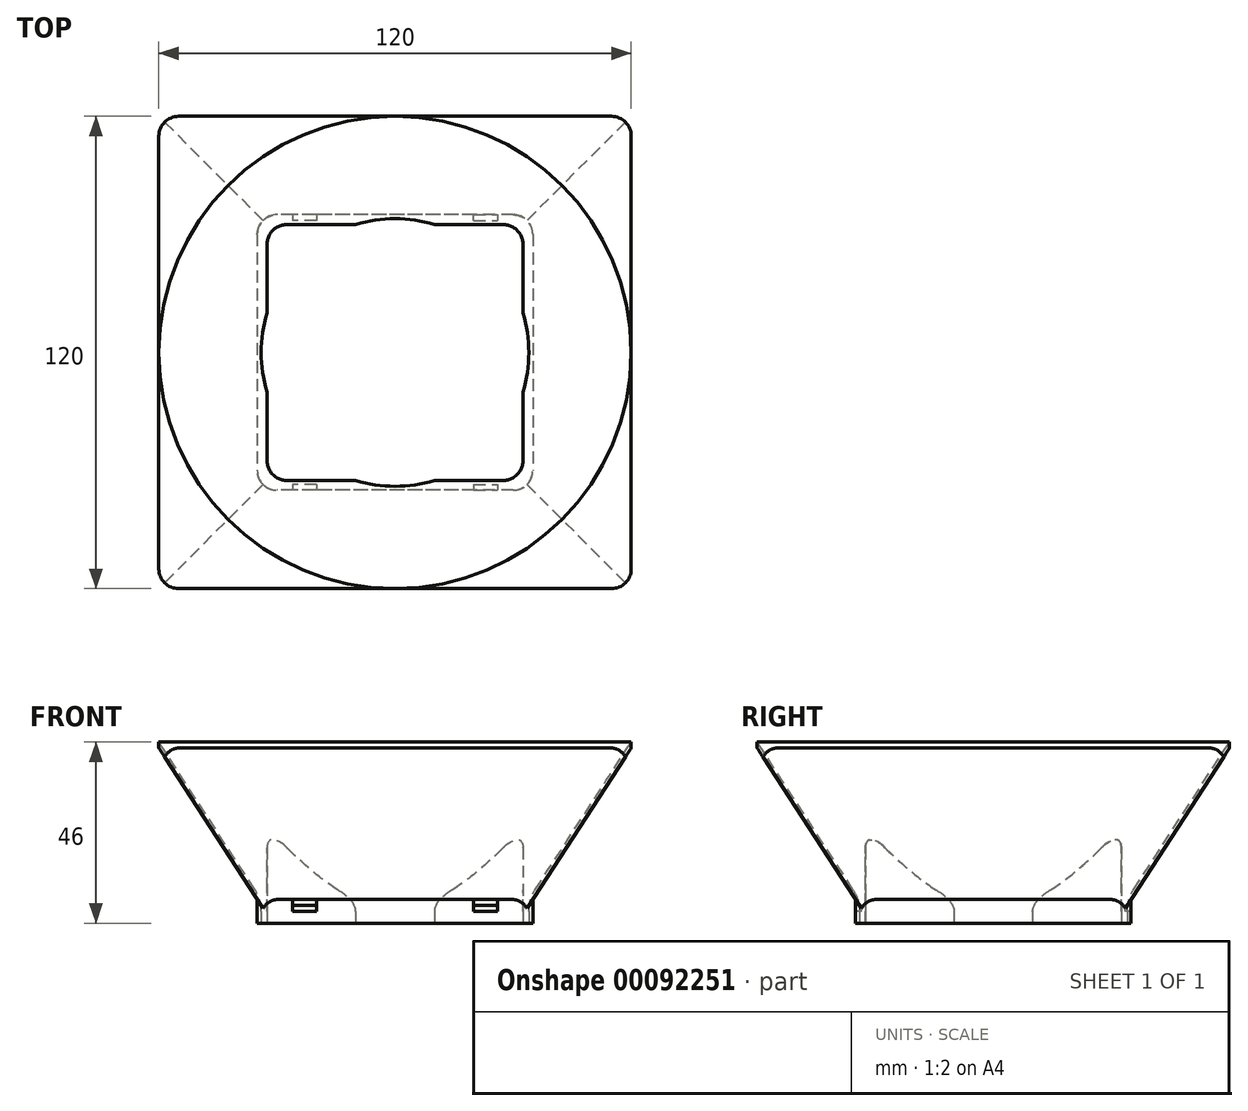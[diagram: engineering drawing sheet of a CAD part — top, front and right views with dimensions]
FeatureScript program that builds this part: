
annotation { "Feature Type Name" : "Feature", "Feature Type Description" : "" }
export const myFeature = defineFeature(function(context is Context, id is Id, definition is map)
    precondition{}
    {
        {
            var Q0;
            Q0=qCreatedBy(makeId("Top.planeOp"),FACE);
            var sketch = newSketch(context, id + "F0", { "sketchPlane" : qUnion([Q0])});
            skLineSegment(sketch, "E0.bottom", {"start": v(35, 35) * mm, "end": v(-35, 35) * mm});
            skLineSegment(sketch, "E0.top", {"start": v(35, -35) * mm, "end": v(-35, -35) * mm});
            skLineSegment(sketch, "E0.left", {"start": v(35, 35) * mm, "end": v(35, -35) * mm});
            skLineSegment(sketch, "E0.right", {"start": v(-35, 35) * mm, "end": v(-35, -35) * mm});
            skPoint(sketch, "E0.middle", {"position": v(0, 0) * mm});
            skSolve(sketch);
        }
        {
            var Q0;
            Q0 = qSketchRegion(id + "F0", true);
            extrude(context, id + "F1", {"entities" : qUnion([Q0]), "depth" : 6 * mm});
        }
        {
            var Q0;
            Q0=makeQuery(id+"F1.opExtrude","CAP_FACE",FACE,{"disambiguationData":[OSD([sQuery(id+"F0.wireOp",EDGE,"E0.bottom"),sQuery(id+"F0.wireOp",EDGE,"E0.top"),sQuery(id+"F0.wireOp",EDGE,"E0.left"),sQuery(id+"F0.wireOp",EDGE,"E0.right")])],"isStart":true});
            var sketch = newSketch(context, id + "F2", { "sketchPlane" : qUnion([Q0])});
            skPoint(sketch, "E1", {"position": v(0, 0) * mm});
            skSolve(sketch);
        }
        {
            var Q0;
            Q0=sQuery(id+"F2.wireOp",VERTEX,"E1");
            var Q1;
            Q1=makeQuery(id+"F1.opExtrude","SWEPT_BODY",BODY,{"disambiguationData":[OSD([sQuery(id+"F0.wireOp",EDGE,"E0.bottom"),sQuery(id+"F0.wireOp",EDGE,"E0.top"),sQuery(id+"F0.wireOp",EDGE,"E0.left"),sQuery(id+"F0.wireOp",EDGE,"E0.right")])]});
            hole(context, id + "F3", {"style" : HoleStyle.SIMPLE, "endStyle" : HoleEndStyle.THROUGH, "holeDiameter" : 68 * mm, "locations" : qUnion([Q0]), "scope" : qUnion([Q1]), "isTappedThrough" : true});
        }
        {
            var Q0;
            Q0=makeQuery(id+"F1.opExtrude","CAP_FACE",FACE,{"disambiguationData":[OSD([sQuery(id+"F0.wireOp",EDGE,"E0.bottom"),sQuery(id+"F0.wireOp",EDGE,"E0.top"),sQuery(id+"F0.wireOp",EDGE,"E0.left"),sQuery(id+"F0.wireOp",EDGE,"E0.right")])],"isStart":false});
            var sketch = newSketch(context, id + "F4", { "sketchPlane" : qUnion([Q0])});
            skLineSegment(sketch, "E2.bottom", {"start": v(-60, -60) * mm, "end": v(60, -60) * mm});
            skLineSegment(sketch, "E2.top", {"start": v(-60, 60) * mm, "end": v(60, 60) * mm});
            skLineSegment(sketch, "E2.left", {"start": v(-60, -60) * mm, "end": v(-60, 60) * mm});
            skLineSegment(sketch, "E2.right", {"start": v(60, -60) * mm, "end": v(60, 60) * mm});
            skPoint(sketch, "E2.middle", {"position": v(0, 0) * mm});
            skSolve(sketch);
        }
        {
            var Q0;
            Q0=makeQuery(id+"F4.imprint","IMPRINT",FACE,{"disambiguationData":[TD([[makeQuery(id+"F4.imprint","IMPRINT",EDGE,{"derivedFrom":sQuery(id+"F4.wireOp",EDGE,"E2.bottom")}),1.0]])]});
            var Q1;
            {var subQ3=sQuery(id+"F0.wireOp",EDGE,"E0.bottom");Q1=makeQuery(id+"F4.imprint","IMPRINT",FACE,{"disambiguationData":[TD([[makeQuery(id+"F4.imprint","IMPRINT",EDGE,{"derivedFrom":makeQuery(id+"F1.opExtrude","CAP_EDGE",EDGE,{"disambiguationData":[OSD([subQ3])],"isStart":false})}),1.0]])]});}
            extrude(context, id + "F5", {"entities" : qUnion([Q0, Q1]), "operationType" : NewBodyOperationType.ADD, "depth" : 40 * mm});
        }
        {
            var Q0;
            Q0=makeQuery(id+"F5.opExtrude","CAP_EDGE",EDGE,{"disambiguationData":[OSD([sQuery(id+"F4.wireOp",EDGE,"E2.bottom")])],"isStart":true});
            var Q1;
            Q1=makeQuery(id+"F5.opExtrude","CAP_EDGE",EDGE,{"disambiguationData":[OSD([sQuery(id+"F4.wireOp",EDGE,"E2.right")])],"isStart":true});
            var Q2;
            Q2=makeQuery(id+"F5.opExtrude","CAP_EDGE",EDGE,{"disambiguationData":[OSD([sQuery(id+"F4.wireOp",EDGE,"E2.top")])],"isStart":true});
            var Q3;
            Q3=makeQuery(id+"F5.opExtrude","CAP_EDGE",EDGE,{"disambiguationData":[OSD([sQuery(id+"F4.wireOp",EDGE,"E2.left")])],"isStart":true});
            chamfer(context, id + "F6", {"entities" : qUnion([Q0, Q1, Q2, Q3]), "chamferType" : ChamferType.TWO_OFFSETS, "width1" : 38.5 * mm, "oppositeDirection" : false, "width2" : 25 * mm, "tangentPropagation" : true});
        }
        {
            var Q0;
            Q0=makeQuery(id+"F5.opExtrude","CAP_EDGE",EDGE,{"disambiguationData":[OSD([sQuery(id+"F0.wireOp",EDGE,"E0.bottom"),sQuery(id+"F0.wireOp",EDGE,"E0.top"),sQuery(id+"F0.wireOp",EDGE,"E0.left"),sQuery(id+"F0.wireOp",EDGE,"E0.right"),sQuery(id+"F3.hole-0.sketch.wireOp",EDGE,"core_line_2")])],"isStart":false});
            chamfer(context, id + "F7", {"entities" : qUnion([Q0]), "chamferType" : ChamferType.TWO_OFFSETS, "width1" : 26 * mm, "oppositeDirection" : false, "width2" : 40 * mm, "tangentPropagation" : true});
        }
        {
            var Q0;
            {var subQ0=sQuery(id+"F3.hole-0.sketch.wireOp",EDGE,"core_line_2");var subQ1=sQuery(id+"F0.wireOp",EDGE,"E0.right");var subQ2=sQuery(id+"F0.wireOp",EDGE,"E0.left");var subQ3=sQuery(id+"F0.wireOp",EDGE,"E0.top");var subQ4=sQuery(id+"F0.wireOp",EDGE,"E0.bottom");Q0=makeQuery(id+"F7.opChamfer","BLEND_EDGE",EDGE,{"blendedFrom":[makeQuery(id+"F5.opExtrude","CAP_EDGE",EDGE,{"disambiguationData":[OSD([subQ4,subQ3,subQ2,subQ1,subQ0])],"isStart":false}),makeQuery(id+"F5.boolean.opBoolean","MERGE",FACE,{"derivedFrom":[makeQuery(id+"F3.hole-0.boolean.opBoolean","COPY",FACE,{"derivedFrom":makeQuery(id+"F3.hole-0.opRevolve","SWEPT_FACE",FACE,{"disambiguationData":[OSD([subQ0])]})}),makeQuery(id+"F5.opExtrude","SWEPT_FACE",FACE,{"disambiguationData":[OSD([subQ4,subQ3,subQ2,subQ1,subQ0])]})]})],"blendedInto":[makeQuery(id+"F5.boolean.opBoolean","MERGE",FACE,{"derivedFrom":[makeQuery(id+"F3.hole-0.boolean.opBoolean","COPY",FACE,{"derivedFrom":makeQuery(id+"F3.hole-0.opRevolve","SWEPT_FACE",FACE,{"disambiguationData":[OSD([subQ0])]})}),makeQuery(id+"F5.opExtrude","SWEPT_FACE",FACE,{"disambiguationData":[OSD([subQ4,subQ3,subQ2,subQ1,subQ0])]})]})]});}
            fillet(context, id + "F8", {"entities" : qUnion([Q0]), "radius" : 10 * mm, "tangentPropagation" : true, "allowEdgeOverflow" : false});
        }
        {
            var Q0;
            Q0=makeQuery(id+"F1.opExtrude","SWEPT_FACE",FACE,{"disambiguationData":[OSD([sQuery(id+"F0.wireOp",EDGE,"E0.top")])]});
            var sketch = newSketch(context, id + "F9", { "sketchPlane" : qUnion([Q0])});
            skLineSegment(sketch, "E3.bottom", {"start": v(-20, 3) * mm, "end": v(-26, 3) * mm});
            skLineSegment(sketch, "E3.top", {"start": v(-20, 6) * mm, "end": v(-26, 6) * mm});
            skLineSegment(sketch, "E3.left", {"start": v(-20, 3) * mm, "end": v(-20, 6) * mm});
            skLineSegment(sketch, "E3.right", {"start": v(-26, 3) * mm, "end": v(-26, 6) * mm});
            skPoint(sketch, "E3.middle", {"position": v(-23, 4.5) * mm});
            skLineSegment(sketch, "E4.bottom", {"start": v(20, 3) * mm, "end": v(26, 3) * mm});
            skLineSegment(sketch, "E4.top", {"start": v(20, 6) * mm, "end": v(26, 6) * mm});
            skLineSegment(sketch, "E4.left", {"start": v(20, 3) * mm, "end": v(20, 6) * mm});
            skLineSegment(sketch, "E4.right", {"start": v(26, 3) * mm, "end": v(26, 6) * mm});
            skPoint(sketch, "E4.middle", {"position": v(23, 4.5) * mm});
            skSolve(sketch);
        }
        {
            var Q0;
            Q0=makeQuery(id+"F9.imprint","IMPRINT",FACE,{"disambiguationData":[TD([[makeQuery(id+"F9.imprint","IMPRINT",EDGE,{"derivedFrom":sQuery(id+"F9.wireOp",EDGE,"E3.bottom")}),-1.0]])]});
            var Q1;
            Q1=makeQuery(id+"F9.imprint","IMPRINT",FACE,{"disambiguationData":[TD([[makeQuery(id+"F9.imprint","IMPRINT",EDGE,{"derivedFrom":sQuery(id+"F9.wireOp",EDGE,"E4.bottom")}),1.0]])]});
            extrude(context, id + "F10", {"entities" : qUnion([Q0, Q1]), "operationType" : NewBodyOperationType.REMOVE, "oppositeDirection" : true, "depth" : 1.5 * mm});
        }
        {
            var Q0;
            Q0=makeQuery(id+"F10.boolean.opBoolean","COPY",FACE,{"derivedFrom":makeQuery(id+"F10.opExtrude","CAP_FACE",FACE,{"disambiguationData":[OSD([sQuery(id+"F9.wireOp",EDGE,"E3.bottom"),sQuery(id+"F9.wireOp",EDGE,"E3.top"),sQuery(id+"F9.wireOp",EDGE,"E3.left"),sQuery(id+"F9.wireOp",EDGE,"E3.right")])],"isStart":false})});
            var Q1;
            Q1=makeQuery(id+"F10.boolean.opBoolean","COPY",FACE,{"derivedFrom":makeQuery(id+"F10.opExtrude","CAP_FACE",FACE,{"disambiguationData":[OSD([sQuery(id+"F9.wireOp",EDGE,"E4.bottom"),sQuery(id+"F9.wireOp",EDGE,"E4.top"),sQuery(id+"F9.wireOp",EDGE,"E4.left"),sQuery(id+"F9.wireOp",EDGE,"E4.right")])],"isStart":false})});
            extrude(context, id + "F11", {"entities" : qUnion([Q0, Q1]), "operationType" : NewBodyOperationType.REMOVE, "oppositeDirection" : true, "depth" : 70 * mm, "hasSecondDirection" : true, "secondDirectionOppositeDirection" : true, "secondDirectionDepth" : 67 * mm});
        }
        {
            var Q0;
            Q0=makeQuery(id+"F1.opExtrude","CAP_FACE",FACE,{"disambiguationData":[OSD([sQuery(id+"F0.wireOp",EDGE,"E0.bottom"),sQuery(id+"F0.wireOp",EDGE,"E0.top"),sQuery(id+"F0.wireOp",EDGE,"E0.left"),sQuery(id+"F0.wireOp",EDGE,"E0.right")])],"isStart":true});
            var sketch = newSketch(context, id + "F12", { "sketchPlane" : qUnion([Q0])});
            skLineSegment(sketch, "E5.bottom", {"start": v(-27.5, -32.5) * mm, "end": v(27.5, -32.5) * mm});
            skLineSegment(sketch, "E5.top", {"start": v(-27.5, 32.5) * mm, "end": v(27.5, 32.5) * mm});
            skLineSegment(sketch, "E5.left", {"start": v(-32.5, -27.5) * mm, "end": v(-32.5, 27.5) * mm});
            skLineSegment(sketch, "E5.right", {"start": v(32.5, -27.5) * mm, "end": v(32.5, 27.5) * mm});
            skPoint(sketch, "E5.middle", {"position": v(0, 0) * mm});
            skPoint(sketch, "E6.visualSharp", {"position": v(-32.5, 32.5) * mm});
            skArc(sketch, "E6.filletArc", {"start": v(-27.5, 32.5) * mm, "mid": v(-31.04, 31.04) * mm, "end": v(-32.5, 27.5) * mm});
            skPoint(sketch, "E7.visualSharp", {"position": v(32.5, 32.5) * mm});
            skArc(sketch, "E7.filletArc", {"start": v(32.5, 27.5) * mm, "mid": v(31.04, 31.04) * mm, "end": v(27.5, 32.5) * mm});
            skPoint(sketch, "E8.visualSharp", {"position": v(32.5, -32.5) * mm});
            skArc(sketch, "E8.filletArc", {"start": v(27.5, -32.5) * mm, "mid": v(31.04, -31.04) * mm, "end": v(32.5, -27.5) * mm});
            skPoint(sketch, "E9.visualSharp", {"position": v(-32.5, -32.5) * mm});
            skArc(sketch, "E9.filletArc", {"start": v(-32.5, -27.5) * mm, "mid": v(-31.04, -31.04) * mm, "end": v(-27.5, -32.5) * mm});
            skSolve(sketch);
        }
        {
            var Q0;
            {var subQ0=sQuery(id+"F12.wireOp",EDGE,"E6.filletArc");Q0=makeQuery(id+"F12.imprint","IMPRINT",FACE,{"disambiguationData":[TD([[makeQuery(id+"F12.imprint","IMPRINT",EDGE,{"derivedFrom":subQ0}),1.0]])]});}
            var Q1;
            {var subQ0=sQuery(id+"F12.wireOp",EDGE,"E7.filletArc");Q1=makeQuery(id+"F12.imprint","IMPRINT",FACE,{"disambiguationData":[TD([[makeQuery(id+"F12.imprint","IMPRINT",EDGE,{"derivedFrom":subQ0}),1.0]])]});}
            var Q2;
            {var subQ0=sQuery(id+"F12.wireOp",EDGE,"E8.filletArc");Q2=makeQuery(id+"F12.imprint","IMPRINT",FACE,{"disambiguationData":[TD([[makeQuery(id+"F12.imprint","IMPRINT",EDGE,{"derivedFrom":subQ0}),1.0]])]});}
            var Q3;
            {var subQ0=sQuery(id+"F12.wireOp",EDGE,"E9.filletArc");Q3=makeQuery(id+"F12.imprint","IMPRINT",FACE,{"disambiguationData":[TD([[makeQuery(id+"F12.imprint","IMPRINT",EDGE,{"derivedFrom":subQ0}),1.0]])]});}
            extrude(context, id + "F13", {"entities" : qUnion([Q0, Q1, Q2, Q3]), "operationType" : NewBodyOperationType.REMOVE, "endBound" : BoundingType.THROUGH_ALL, "oppositeDirection" : true, "depth" : 25 * mm});
        }
        {
            var Q0;
            {var subQ0=sQuery(id+"F12.wireOp",EDGE,"E5.top");var subQ1=sQuery(id+"F3.hole-0.sketch.wireOp",EDGE,"core_line_3");var subQ2=sQuery(id+"F3.hole-0.sketch.wireOp",EDGE,"core_line_2");Q0=makeQuery(id+"F13.boolean.opBoolean","COPY",EDGE,{"derivedFrom":makeQuery(id+"F13.opExtrude","SWEPT_EDGE",EDGE,{"disambiguationData":[OSD([subQ2,subQ1,subQ0]),TDD([makeQuery(id+"F12.imprint","INTERSECT",VERTEX,{"disambiguationData":[OD(1.0)],"derivedFrom":[makeQuery(id+"F3.hole-0.boolean.opBoolean","COPY",EDGE,{"derivedFrom":makeQuery(id+"F3.hole-0.opRevolve","SWEPT_EDGE",EDGE,{"disambiguationData":[OSD([subQ2,subQ1])]})}),subQ0]})])]})});}
            var Q1;
            {var subQ0=sQuery(id+"F12.wireOp",EDGE,"E5.top");var subQ1=sQuery(id+"F3.hole-0.sketch.wireOp",EDGE,"core_line_3");var subQ2=sQuery(id+"F3.hole-0.sketch.wireOp",EDGE,"core_line_2");Q1=makeQuery(id+"F13.boolean.opBoolean","COPY",EDGE,{"derivedFrom":makeQuery(id+"F13.opExtrude","SWEPT_EDGE",EDGE,{"disambiguationData":[OSD([subQ2,subQ1,subQ0]),TDD([makeQuery(id+"F12.imprint","INTERSECT",VERTEX,{"disambiguationData":[OD(0.0)],"derivedFrom":[makeQuery(id+"F3.hole-0.boolean.opBoolean","COPY",EDGE,{"derivedFrom":makeQuery(id+"F3.hole-0.opRevolve","SWEPT_EDGE",EDGE,{"disambiguationData":[OSD([subQ2,subQ1])]})}),subQ0]})])]})});}
            var Q2;
            {var subQ0=sQuery(id+"F12.wireOp",EDGE,"E5.right");var subQ1=sQuery(id+"F3.hole-0.sketch.wireOp",EDGE,"core_line_3");var subQ2=sQuery(id+"F3.hole-0.sketch.wireOp",EDGE,"core_line_2");Q2=makeQuery(id+"F13.boolean.opBoolean","COPY",EDGE,{"derivedFrom":makeQuery(id+"F13.opExtrude","SWEPT_EDGE",EDGE,{"disambiguationData":[OSD([subQ2,subQ1,subQ0]),TDD([makeQuery(id+"F12.imprint","INTERSECT",VERTEX,{"disambiguationData":[OD(0.0)],"derivedFrom":[makeQuery(id+"F3.hole-0.boolean.opBoolean","COPY",EDGE,{"derivedFrom":makeQuery(id+"F3.hole-0.opRevolve","SWEPT_EDGE",EDGE,{"disambiguationData":[OSD([subQ2,subQ1])]})}),subQ0]})])]})});}
            var Q3;
            {var subQ0=sQuery(id+"F12.wireOp",EDGE,"E5.bottom");var subQ1=sQuery(id+"F3.hole-0.sketch.wireOp",EDGE,"core_line_3");var subQ2=sQuery(id+"F3.hole-0.sketch.wireOp",EDGE,"core_line_2");Q3=makeQuery(id+"F13.boolean.opBoolean","COPY",EDGE,{"derivedFrom":makeQuery(id+"F13.opExtrude","SWEPT_EDGE",EDGE,{"disambiguationData":[OSD([subQ2,subQ1,subQ0]),TDD([makeQuery(id+"F12.imprint","INTERSECT",VERTEX,{"disambiguationData":[OD(0.0)],"derivedFrom":[makeQuery(id+"F3.hole-0.boolean.opBoolean","COPY",EDGE,{"derivedFrom":makeQuery(id+"F3.hole-0.opRevolve","SWEPT_EDGE",EDGE,{"disambiguationData":[OSD([subQ2,subQ1])]})}),subQ0]})])]})});}
            fillet(context, id + "F14", {"entities" : qUnion([Q0, Q1, Q2, Q3]), "radius" : 10 * mm, "tangentPropagation" : true, "allowEdgeOverflow" : false});
        }
        {
            var Q0;
            Q0=makeQuery(id+"F10.boolean.opBoolean","COPY",EDGE,{"derivedFrom":makeQuery(id+"F10.opExtrude","CAP_EDGE",EDGE,{"disambiguationData":[OSD([sQuery(id+"F9.wireOp",EDGE,"E3.top")])],"isStart":false})});
            var Q1;
            Q1=makeQuery(id+"F10.boolean.opBoolean","COPY",EDGE,{"derivedFrom":makeQuery(id+"F10.opExtrude","CAP_EDGE",EDGE,{"disambiguationData":[OSD([sQuery(id+"F9.wireOp",EDGE,"E4.top")])],"isStart":false})});
            var Q2;
            Q2=makeQuery(id+"F11.boolean.opBoolean","COPY",EDGE,{"derivedFrom":makeQuery(id+"F11.opExtrude","CAP_EDGE",EDGE,{"disambiguationData":[OSD([sQuery(id+"F9.wireOp",EDGE,"E3.top")])],"isStart":true})});
            var Q3;
            Q3=makeQuery(id+"F11.boolean.opBoolean","COPY",EDGE,{"derivedFrom":makeQuery(id+"F11.opExtrude","CAP_EDGE",EDGE,{"disambiguationData":[OSD([sQuery(id+"F9.wireOp",EDGE,"E4.top")])],"isStart":true})});
            chamfer(context, id + "F15", {"entities" : qUnion([Q0, Q1, Q2, Q3]), "width" : 1.5 * mm, "tangentPropagation" : true});
        }
        {
            var Q0;
            Q0=makeQuery(id+"F5.opExtrude","SWEPT_EDGE",EDGE,{"disambiguationData":[OSD([sQuery(id+"F4.wireOp",EDGE,"E2.bottom"),sQuery(id+"F4.wireOp",EDGE,"E2.left")])]});
            var Q1;
            Q1=makeQuery(id+"F5.opExtrude","SWEPT_EDGE",EDGE,{"disambiguationData":[OSD([sQuery(id+"F4.wireOp",EDGE,"E2.bottom"),sQuery(id+"F4.wireOp",EDGE,"E2.right")])]});
            var Q2;
            Q2=makeQuery(id+"F5.opExtrude","SWEPT_EDGE",EDGE,{"disambiguationData":[OSD([sQuery(id+"F4.wireOp",EDGE,"E2.top"),sQuery(id+"F4.wireOp",EDGE,"E2.right")])]});
            var Q3;
            Q3=makeQuery(id+"F5.opExtrude","SWEPT_EDGE",EDGE,{"disambiguationData":[OSD([sQuery(id+"F4.wireOp",EDGE,"E2.top"),sQuery(id+"F4.wireOp",EDGE,"E2.left")])]});
            var Q4;
            Q4=makeQuery(id+"F1.opExtrude","SWEPT_EDGE",EDGE,{"disambiguationData":[OSD([sQuery(id+"F0.wireOp",EDGE,"E0.bottom"),sQuery(id+"F0.wireOp",EDGE,"E0.right")])]});
            var Q5;
            Q5=makeQuery(id+"F1.opExtrude","SWEPT_EDGE",EDGE,{"disambiguationData":[OSD([sQuery(id+"F0.wireOp",EDGE,"E0.top"),sQuery(id+"F0.wireOp",EDGE,"E0.right")])]});
            var Q6;
            Q6=makeQuery(id+"F1.opExtrude","SWEPT_EDGE",EDGE,{"disambiguationData":[OSD([sQuery(id+"F0.wireOp",EDGE,"E0.top"),sQuery(id+"F0.wireOp",EDGE,"E0.left")])]});
            var Q7;
            Q7=makeQuery(id+"F1.opExtrude","SWEPT_EDGE",EDGE,{"disambiguationData":[OSD([sQuery(id+"F0.wireOp",EDGE,"E0.bottom"),sQuery(id+"F0.wireOp",EDGE,"E0.left")])]});
            fillet(context, id + "F16", {"entities" : qUnion([Q0, Q1, Q2, Q3, Q4, Q5, Q6, Q7]), "radius" : 5 * mm, "allowEdgeOverflow" : false});
        }
    });
